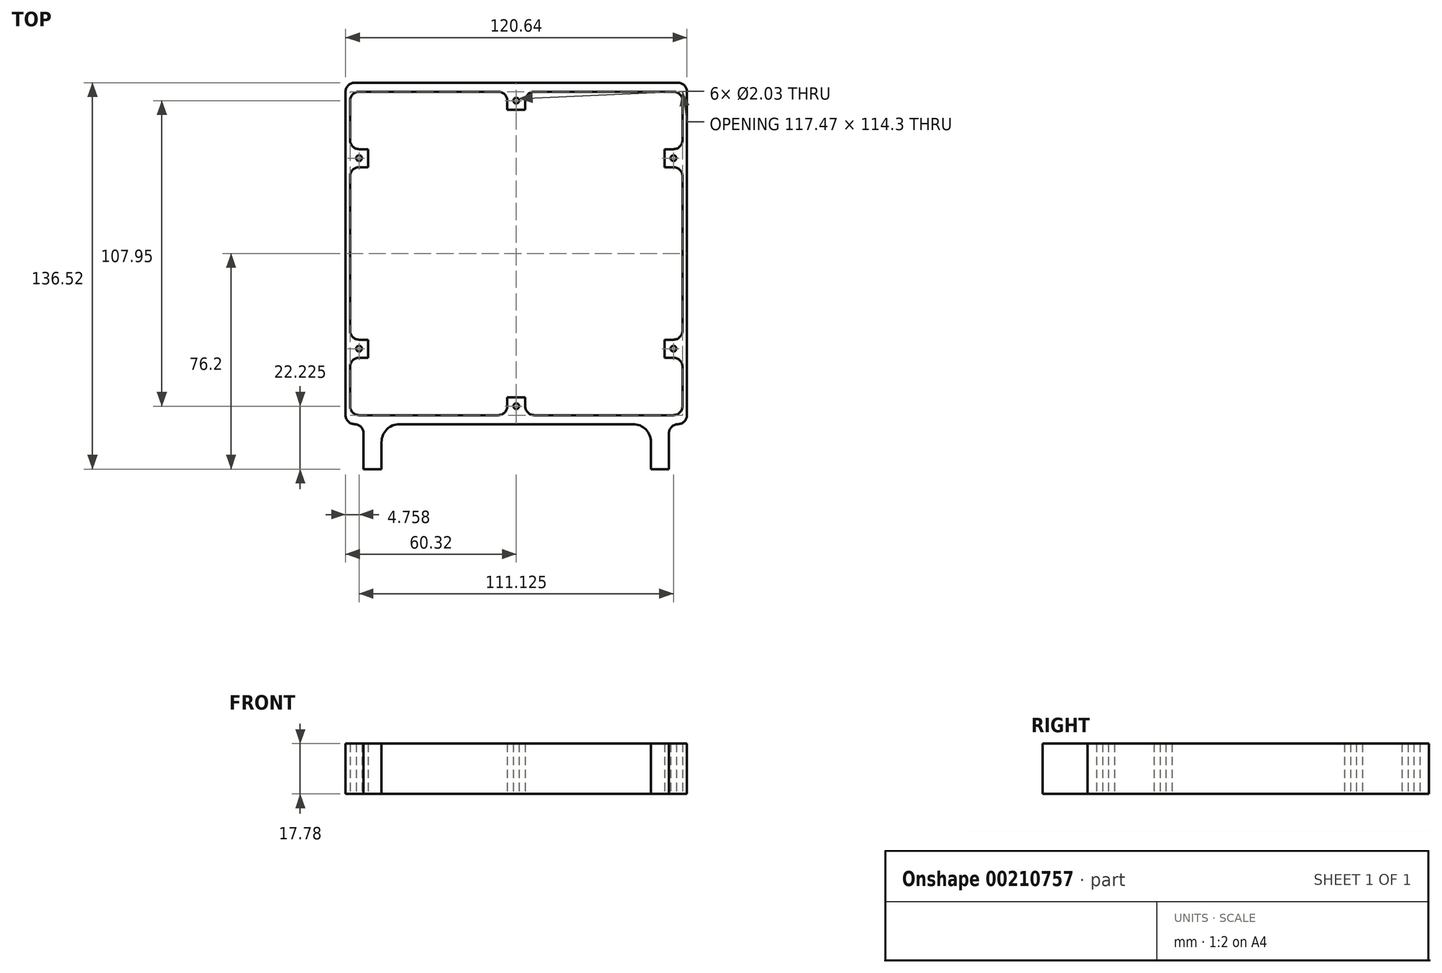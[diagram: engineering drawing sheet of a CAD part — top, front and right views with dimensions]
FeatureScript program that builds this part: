
annotation { "Feature Type Name" : "Feature", "Feature Type Description" : "" }
export const myFeature = defineFeature(function(context is Context, id is Id, definition is map)
    precondition{}
    {
        {
            var Q0;
            Q0=qCreatedBy(makeId("Top.planeOp"),FACE);
            var sketch = newSketch(context, id + "F0", { "sketchPlane" : qUnion([Q0])});
            skLineSegment(sketch, "E0.bottom", {"start": v(-57.15, 60.32) * mm, "end": v(57.15, 60.33) * mm});
            skLineSegment(sketch, "E0.top", {"start": v(-57.15, -60.33) * mm, "end": v(-57.15, -60.33) * mm});
            skLineSegment(sketch, "E0.left", {"start": v(-60.33, 57.15) * mm, "end": v(-60.33, -57.15) * mm});
            skLineSegment(sketch, "E0.right", {"start": v(60.33, 57.15) * mm, "end": v(60.33, -57.15) * mm});
            skPoint(sketch, "E1.visualSharp", {"position": v(-60.33, 60.32) * mm});
            skArc(sketch, "E1.filletArc", {"start": v(-57.15, 60.32) * mm, "mid": v(-59.4, 59.4) * mm, "end": v(-60.33, 57.15) * mm});
            skPoint(sketch, "E2.visualSharp", {"position": v(60.33, 60.33) * mm});
            skArc(sketch, "E2.filletArc", {"start": v(60.33, 57.15) * mm, "mid": v(59.4, 59.4) * mm, "end": v(57.15, 60.33) * mm});
            skPoint(sketch, "E3.visualSharp", {"position": v(60.33, -60.33) * mm});
            skArc(sketch, "E3.filletArc", {"start": v(57.15, -60.33) * mm, "mid": v(59.4, -59.4) * mm, "end": v(60.33, -57.15) * mm});
            skPoint(sketch, "E4.visualSharp", {"position": v(-60.33, -60.33) * mm});
            skArc(sketch, "E4.filletArc", {"start": v(-60.33, -57.15) * mm, "mid": v(-59.4, -59.4) * mm, "end": v(-57.15, -60.33) * mm});
            skLineSegment(sketch, "E5.bottom", {"start": v(-55.56, 57.15) * mm, "end": v(-6.35, 57.15) * mm});
            skLineSegment(sketch, "E5.top", {"start": v(-55.56, -57.15) * mm, "end": v(-6.35, -57.15) * mm});
            skLineSegment(sketch, "E5.left", {"start": v(-58.74, 53.98) * mm, "end": v(-58.74, 40) * mm});
            skLineSegment(sketch, "E5.right", {"start": v(58.74, 53.98) * mm, "end": v(58.74, 40) * mm});
            skPoint(sketch, "E6.visualSharp", {"position": v(-58.74, 57.15) * mm});
            skArc(sketch, "E6.filletArc", {"start": v(-55.56, 57.15) * mm, "mid": v(-57.8, 56.22) * mm, "end": v(-58.74, 53.98) * mm});
            skPoint(sketch, "E7.visualSharp", {"position": v(58.74, 57.15) * mm});
            skArc(sketch, "E7.filletArc", {"start": v(58.74, 53.98) * mm, "mid": v(57.8, 56.22) * mm, "end": v(55.56, 57.15) * mm});
            skPoint(sketch, "E8.visualSharp", {"position": v(-58.74, -57.15) * mm});
            skArc(sketch, "E8.filletArc", {"start": v(-58.74, -53.98) * mm, "mid": v(-57.8, -56.22) * mm, "end": v(-55.56, -57.15) * mm});
            skPoint(sketch, "E9.visualSharp", {"position": v(58.74, -57.15) * mm});
            skArc(sketch, "E9.filletArc", {"start": v(55.56, -57.15) * mm, "mid": v(57.8, -56.22) * mm, "end": v(58.74, -53.98) * mm});
            skLineSegment(sketch, "E10.top", {"start": v(-53.97, -76.2) * mm, "end": v(-47.62, -76.2) * mm});
            skLineSegment(sketch, "E10.left", {"start": v(-53.97, -63.5) * mm, "end": v(-53.97, -76.2) * mm});
            skLineSegment(sketch, "E10.right", {"start": v(-47.62, -66.67) * mm, "end": v(-47.62, -76.2) * mm});
            skLineSegment(sketch, "E11.top", {"start": v(53.98, -76.2) * mm, "end": v(47.63, -76.2) * mm});
            skLineSegment(sketch, "E11.left", {"start": v(53.98, -63.5) * mm, "end": v(53.98, -76.2) * mm});
            skLineSegment(sketch, "E11.right", {"start": v(47.63, -66.67) * mm, "end": v(47.63, -76.2) * mm});
            skLineSegment(sketch, "E12.trimOffspring", {"start": v(57.15, -60.33) * mm, "end": v(57.15, -60.33) * mm});
            skLineSegment(sketch, "E13.trimOffspring", {"start": v(-41.28, -60.33) * mm, "end": v(41.28, -60.33) * mm});
            skPoint(sketch, "E14.visualSharp", {"position": v(-47.62, -60.33) * mm});
            skArc(sketch, "E14.filletArc", {"start": v(-41.28, -60.32) * mm, "mid": v(-45.77, -62.18) * mm, "end": v(-47.63, -66.67) * mm});
            skPoint(sketch, "E15.visualSharp", {"position": v(47.63, -60.32) * mm});
            skArc(sketch, "E15.filletArc", {"start": v(47.62, -66.67) * mm, "mid": v(45.77, -62.18) * mm, "end": v(41.27, -60.32) * mm});
            skPoint(sketch, "E16.visualSharp", {"position": v(53.98, -60.33) * mm});
            skArc(sketch, "E16.filletArc", {"start": v(57.15, -60.33) * mm, "mid": v(54.9, -61.25) * mm, "end": v(53.98, -63.5) * mm});
            skPoint(sketch, "E17.visualSharp", {"position": v(-53.97, -60.33) * mm});
            skArc(sketch, "E17.filletArc", {"start": v(-53.97, -63.5) * mm, "mid": v(-54.9, -61.25) * mm, "end": v(-57.15, -60.33) * mm});
            skLineSegment(sketch, "E18.top", {"start": v(-3.18, 50.8) * mm, "end": v(3.17, 50.8) * mm});
            skLineSegment(sketch, "E18.left", {"start": v(-3.18, 53.98) * mm, "end": v(-3.18, 50.8) * mm});
            skLineSegment(sketch, "E18.right", {"start": v(3.17, 53.98) * mm, "end": v(3.17, 50.8) * mm});
            skLineSegment(sketch, "E19.trimOffspring", {"start": v(6.35, 57.15) * mm, "end": v(55.56, 57.15) * mm});
            skLineSegment(sketch, "E20.bottom", {"start": v(-55.56, 36.83) * mm, "end": v(-52.39, 36.83) * mm});
            skLineSegment(sketch, "E20.top", {"start": v(-55.56, 30.48) * mm, "end": v(-52.39, 30.48) * mm});
            skLineSegment(sketch, "E20.right", {"start": v(-52.39, 36.83) * mm, "end": v(-52.39, 30.48) * mm});
            skLineSegment(sketch, "E21.trimOffspring", {"start": v(-58.74, 27.3) * mm, "end": v(-58.74, -27.3) * mm});
            skLineSegment(sketch, "E22.bottom", {"start": v(55.56, 36.83) * mm, "end": v(52.39, 36.83) * mm});
            skLineSegment(sketch, "E22.top", {"start": v(55.56, 30.48) * mm, "end": v(52.39, 30.48) * mm});
            skLineSegment(sketch, "E22.right", {"start": v(52.39, 36.83) * mm, "end": v(52.39, 30.48) * mm});
            skLineSegment(sketch, "E23.trimOffspring", {"start": v(58.74, 27.3) * mm, "end": v(58.74, -27.3) * mm});
            skLineSegment(sketch, "E24.top", {"start": v(-3.17, -50.8) * mm, "end": v(3.18, -50.8) * mm});
            skLineSegment(sketch, "E24.left", {"start": v(-3.18, -53.98) * mm, "end": v(-3.18, -50.8) * mm});
            skLineSegment(sketch, "E24.right", {"start": v(3.17, -53.98) * mm, "end": v(3.17, -50.8) * mm});
            skLineSegment(sketch, "E25.trimOffspring", {"start": v(6.35, -57.15) * mm, "end": v(55.56, -57.15) * mm});
            skLineSegment(sketch, "E26.bottom", {"start": v(-52.39, -30.48) * mm, "end": v(-55.56, -30.48) * mm});
            skLineSegment(sketch, "E26.top", {"start": v(-52.39, -36.83) * mm, "end": v(-55.56, -36.83) * mm});
            skLineSegment(sketch, "E26.left", {"start": v(-52.39, -30.48) * mm, "end": v(-52.39, -36.83) * mm});
            skLineSegment(sketch, "E27.trimOffspring", {"start": v(-58.74, -40) * mm, "end": v(-58.74, -53.98) * mm});
            skLineSegment(sketch, "E28.bottom", {"start": v(55.56, -30.48) * mm, "end": v(52.39, -30.48) * mm});
            skLineSegment(sketch, "E28.top", {"start": v(55.56, -36.83) * mm, "end": v(52.39, -36.83) * mm});
            skLineSegment(sketch, "E28.right", {"start": v(52.39, -30.48) * mm, "end": v(52.39, -36.83) * mm});
            skLineSegment(sketch, "E29.trimOffspring", {"start": v(58.74, -40) * mm, "end": v(58.74, -53.98) * mm});
            skPoint(sketch, "E30.visualSharp", {"position": v(58.74, -30.48) * mm});
            skArc(sketch, "E30.filletArc", {"start": v(55.56, -30.48) * mm, "mid": v(57.8, -29.55) * mm, "end": v(58.74, -27.3) * mm});
            skPoint(sketch, "E31.visualSharp", {"position": v(58.74, -36.83) * mm});
            skArc(sketch, "E31.filletArc", {"start": v(58.74, -40) * mm, "mid": v(57.8, -37.76) * mm, "end": v(55.56, -36.83) * mm});
            skPoint(sketch, "E32.visualSharp", {"position": v(-58.74, -36.83) * mm});
            skArc(sketch, "E32.filletArc", {"start": v(-55.56, -36.83) * mm, "mid": v(-57.8, -37.76) * mm, "end": v(-58.74, -40) * mm});
            skPoint(sketch, "E33.visualSharp", {"position": v(-58.74, -30.48) * mm});
            skArc(sketch, "E33.filletArc", {"start": v(-58.74, -27.3) * mm, "mid": v(-57.8, -29.55) * mm, "end": v(-55.56, -30.48) * mm});
            skPoint(sketch, "E34.visualSharp", {"position": v(58.74, 30.48) * mm});
            skArc(sketch, "E34.filletArc", {"start": v(58.74, 27.3) * mm, "mid": v(57.8, 29.55) * mm, "end": v(55.56, 30.48) * mm});
            skPoint(sketch, "E35.visualSharp", {"position": v(-58.74, 30.48) * mm});
            skArc(sketch, "E35.filletArc", {"start": v(-55.56, 30.48) * mm, "mid": v(-57.8, 29.55) * mm, "end": v(-58.74, 27.3) * mm});
            skPoint(sketch, "E36.visualSharp", {"position": v(58.74, 36.83) * mm});
            skArc(sketch, "E36.filletArc", {"start": v(55.56, 36.83) * mm, "mid": v(57.8, 37.76) * mm, "end": v(58.74, 40) * mm});
            skPoint(sketch, "E37.visualSharp", {"position": v(-58.74, 36.83) * mm});
            skArc(sketch, "E37.filletArc", {"start": v(-58.74, 40) * mm, "mid": v(-57.8, 37.76) * mm, "end": v(-55.56, 36.83) * mm});
            skPoint(sketch, "E38.visualSharp", {"position": v(-3.18, 57.15) * mm});
            skArc(sketch, "E38.filletArc", {"start": v(-3.18, 53.98) * mm, "mid": v(-4.1, 56.22) * mm, "end": v(-6.35, 57.15) * mm});
            skPoint(sketch, "E39.visualSharp", {"position": v(3.17, 57.15) * mm});
            skArc(sketch, "E39.filletArc", {"start": v(6.35, 57.15) * mm, "mid": v(4.1, 56.22) * mm, "end": v(3.17, 53.98) * mm});
            skPoint(sketch, "E40.visualSharp", {"position": v(-3.18, -57.15) * mm});
            skArc(sketch, "E40.filletArc", {"start": v(-6.35, -57.15) * mm, "mid": v(-4.1, -56.22) * mm, "end": v(-3.18, -53.98) * mm});
            skPoint(sketch, "E41.visualSharp", {"position": v(3.17, -57.15) * mm});
            skArc(sketch, "E41.filletArc", {"start": v(3.17, -53.98) * mm, "mid": v(4.1, -56.22) * mm, "end": v(6.35, -57.15) * mm});
            skCircle(sketch, "E42", {"center": v(-55.56, 33.65) * mm, "radius": 1.02 * mm});
            skCircle(sketch, "E43", {"center": v(0, 53.98) * mm, "radius": 1.02 * mm});
            skCircle(sketch, "E44", {"center": v(0, -53.98) * mm, "radius": 1.02 * mm});
            skCircle(sketch, "E45", {"center": v(-55.56, -33.66) * mm, "radius": 1.02 * mm});
            skPoint(sketch, "E45.centerSnap0", {"position": v(-52.39, -33.66) * mm});
            skCircle(sketch, "E46", {"center": v(55.56, -33.66) * mm, "radius": 1.02 * mm});
            skPoint(sketch, "E46.centerSnap0", {"position": v(52.39, -33.66) * mm});
            skCircle(sketch, "E47", {"center": v(55.56, 33.66) * mm, "radius": 1.02 * mm});
            skPoint(sketch, "E47.centerSnap0", {"position": v(52.39, 33.66) * mm});
            skSolve(sketch);
        }
        {
            var Q0;
            Q0 = qSketchRegion(id + "F0", true);
            extrude(context, id + "F1", {"entities" : qUnion([Q0]), "depth" : 17.78 * mm});
        }
    });
